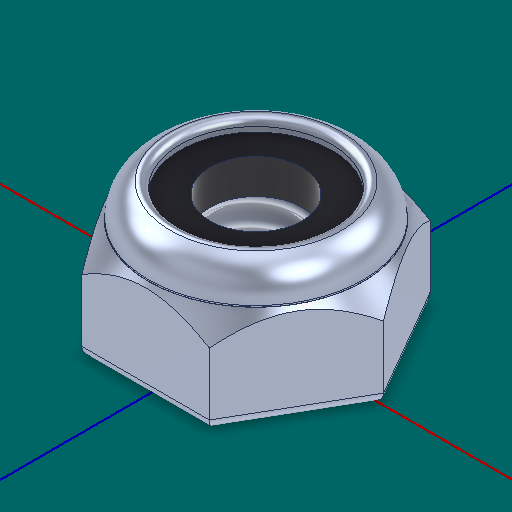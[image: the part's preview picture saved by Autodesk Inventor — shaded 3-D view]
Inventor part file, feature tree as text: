
AUTODESK INVENTOR PART (.ipt)
format: ipt  version: 2025 (Build 290162000, 162)  size: 232,960 bytes
history: native  units: in
note: dims shown in document units (in); Inventor stores cm internally (conversion verified against a paired STEP export)
features: other x4, sketch x2, plane x1
ambient origin geometry x8: Origin, YZ Plane, XZ Plane, XY Plane, X Axis, Y Axis, Z Axis, Center Point
bodies: Body1 (feature_tree)
feature tree (7):
  other  "Nut Thin Nylock.ipt"
  other  "NONE::Nut Thin Nylock.ipt"
  other  "TaggingFeature1"
  sketch  "Sketch1"  dims[d0=0.3937in]
  sketch  "Sketch2"
  plane  "Work Plane1"
  parser-record x1  (decoder bookkeeping rows leaked as tree rows — omitted from the tree; the rows remain in map.json)
